FCSTD DOCUMENT  (FreeCAD 0.20R28811 (Git))
Label: Base Proto
License: All rights reserved
LicenseURL: http://en.wikipedia.org/wiki/All_rights_reserved
objects: Part::Ellipsoid×86, Part::Feature×52, Part::Fillet×44, Part::Cylinder×40, Part::MultiFuse×39, Part::Box×10, App::Part×5, Part::Wedge×1
note: 272 computed .brp shape members not serialized (recipe doc carries the construction recipe); baked Part::Feature solids carry a one-line shape summary decoded from their .brp

FEATURE [Part::Box] Box  label="Base"
  AttacherType = Attacher::AttachEngine3D
  Height = 3
  Length = 180
  Width = 120
FEATURE [Part::Box] Box001  label="Cube001"
  AttacherType = Attacher::AttachEngine3D
  Height = 10
  Length = 43
  Placement = pos=(0,0,3) rot=(0,0,1;0rad)
  Width = 3
FEATURE [Part::Box] Box002  label="Cube"
  AttacherType = Attacher::AttachEngine3D
  Height = 2.7
  Length = 43
  Placement = pos=(0,0,13) rot=(0,0,1;0rad)
  Width = 2
FEATURE [Part::Ellipsoid] Ellipsoid001
  Angle1 = -90
  Angle2 = 90
  Angle3 = 360
  AttacherType = Attacher::AttachEngine3D
  Placement = pos=(11,1.5,14.8) rot=(0,0,1;0rad)
  Radius1 = 0.5
  Radius2 = 4
  Radius3 = 0.75
FEATURE [Part::Ellipsoid] Ellipsoid002
  Angle1 = -90
  Angle2 = 90
  Angle3 = 360
  AttacherType = Attacher::AttachEngine3D
  Placement = pos=(34,1.5,14.8) rot=(0,0,1;0rad)
  Radius1 = 0.5
  Radius2 = 4
  Radius3 = 0.75
FEATURE [Part::MultiFuse] Fusion  label="Pared_RPI4_Nano"
  Refine = true
  Shapes = -> [Ellipsoid002,Box001,Box002,Ellipsoid001]
FEATURE [Part::Box] Box003  label="Cube002"
  AttacherType = Attacher::AttachEngine3D
  Height = 10
  Length = 43
  Placement = pos=(0,0,3) rot=(0,0,1;0rad)
  Width = 3
FEATURE [Part::Box] Box004  label="Cube003"
  AttacherType = Attacher::AttachEngine3D
  Height = 2.7
  Length = 43
  Placement = pos=(0,0,13) rot=(0,0,1;0rad)
  Width = 2
FEATURE [Part::Ellipsoid] Ellipsoid003
  Angle1 = -90
  Angle2 = 90
  Angle3 = 360
  AttacherType = Attacher::AttachEngine3D
  Placement = pos=(11,1.5,14.8) rot=(0,0,1;0rad)
  Radius1 = 0.5
  Radius2 = 4
  Radius3 = 0.75
FEATURE [Part::Ellipsoid] Ellipsoid004
  Angle1 = -90
  Angle2 = 90
  Angle3 = 360
  AttacherType = Attacher::AttachEngine3D
  Placement = pos=(34,1.5,14.8) rot=(0,0,1;0rad)
  Radius1 = 0.5
  Radius2 = 4
  Radius3 = 0.75
FEATURE [Part::MultiFuse] Fusion001  label="Pared_RPI4_Nano001"
  Placement = pos=(43,22,0) rot=(0,0,1;3.14159rad)
  Refine = true
  Shapes = -> [Ellipsoid004,Box003,Box004,Ellipsoid003]
FEATURE [Part::Cylinder] Cylinder001
  Angle = 360
  AttacherType = Attacher::AttachEngine3D
  FirstAngle = 0
  Height = 10
  Placement = pos=(4,4,-2) rot=(0,0,1;0rad)
  Radius = 4
  SecondAngle = 0
FEATURE [Part::Fillet] Fillet
  Base = -> Cylinder001
  Edges = 1 edges r=1: [Edge3]
  Placement = pos=(0,0,5) rot=(0,0,1;0rad)
FEATURE [Part::Cylinder] Cylinder002
  Angle = 360
  AttacherType = Attacher::AttachEngine3D
  FirstAngle = 0
  Height = 6
  Placement = pos=(5,5,18) rot=(0,0,1;0rad)
  Radius = 1.5
  SecondAngle = 0
FEATURE [Part::Cylinder] Cylinder003
  Angle = 360
  AttacherType = Attacher::AttachEngine3D
  FirstAngle = 0
  Height = 10
  Placement = pos=(4,4,-2) rot=(0,0,1;0rad)
  Radius = 4
  SecondAngle = 0
FEATURE [Part::Ellipsoid] Ellipsoid009
  Angle1 = -90
  Angle2 = 90
  Angle3 = 360
  AttacherType = Attacher::AttachEngine3D
  Placement = pos=(5,4,22) rot=(0,1,0;1.5708rad)
  Radius1 = 0.5
  Radius2 = 2
  Radius3 = 0.75
FEATURE [Part::Ellipsoid] Ellipsoid010
  Angle1 = -90
  Angle2 = 90
  Angle3 = 360
  AttacherType = Attacher::AttachEngine3D
  Placement = pos=(4,5,22) rot=(0.57735,-0.57735,-0.57735;4.18879rad)
  Radius1 = 0.5
  Radius2 = 2
  Radius3 = 0.75
FEATURE [Part::Ellipsoid] Ellipsoid011
  Angle1 = -90
  Angle2 = 90
  Angle3 = 360
  AttacherType = Attacher::AttachEngine3D
  Placement = pos=(5,6,22) rot=(0,1,0;1.5708rad)
  Radius1 = 0.5
  Radius2 = 2
  Radius3 = 0.75
FEATURE [Part::Ellipsoid] Ellipsoid012
  Angle1 = -90
  Angle2 = 90
  Angle3 = 360
  AttacherType = Attacher::AttachEngine3D
  Placement = pos=(6,5,22) rot=(0.57735,-0.57735,-0.57735;4.18879rad)
  Radius1 = 0.5
  Radius2 = 2
  Radius3 = 0.75
FEATURE [Part::Fillet] Fillet002
  Base = -> Cylinder003
  Edges = 1 edges r=1: [Edge3]
  Placement = pos=(0,0,5) rot=(0,0,1;0rad)
FEATURE [Part::MultiFuse] Fusion006
  Placement = pos=(-1,-1,-10) rot=(0,0,1;0rad)
  Refine = true
  Shapes = -> [Ellipsoid012,Cylinder002,Ellipsoid009,Ellipsoid010,Ellipsoid011]
FEATURE [Part::Fillet] Fillet003
  Base = -> Fusion006
  Edges = 1 edges r=1: [Edge7]
  Placement = pos=(0,0,4) rot=(0,0,1;0rad)
FEATURE [Part::MultiFuse] Fusion007  label="Pilar_PCB_1.6mm_3mm001"
  Placement = pos=(80,41,0) rot=(0,0,1;0rad)
  Refine = true
  Shapes = -> [Fillet003,Fillet002]
FEATURE [Part::Cylinder] Cylinder004
  Angle = 360
  AttacherType = Attacher::AttachEngine3D
  FirstAngle = 0
  Height = 6
  Placement = pos=(5,5,18) rot=(0,0,1;0rad)
  Radius = 1.5
  SecondAngle = 0
FEATURE [Part::Cylinder] Cylinder005
  Angle = 360
  AttacherType = Attacher::AttachEngine3D
  FirstAngle = 0
  Height = 10
  Placement = pos=(4,4,-2) rot=(0,0,1;0rad)
  Radius = 4
  SecondAngle = 0
FEATURE [Part::Ellipsoid] Ellipsoid013
  Angle1 = -90
  Angle2 = 90
  Angle3 = 360
  AttacherType = Attacher::AttachEngine3D
  Placement = pos=(5,4,22) rot=(0,1,0;1.5708rad)
  Radius1 = 0.5
  Radius2 = 2
  Radius3 = 0.75
FEATURE [Part::Ellipsoid] Ellipsoid014
  Angle1 = -90
  Angle2 = 90
  Angle3 = 360
  AttacherType = Attacher::AttachEngine3D
  Placement = pos=(4,5,22) rot=(0.57735,-0.57735,-0.57735;4.18879rad)
  Radius1 = 0.5
  Radius2 = 2
  Radius3 = 0.75
FEATURE [Part::Ellipsoid] Ellipsoid015
  Angle1 = -90
  Angle2 = 90
  Angle3 = 360
  AttacherType = Attacher::AttachEngine3D
  Placement = pos=(5,6,22) rot=(0,1,0;1.5708rad)
  Radius1 = 0.5
  Radius2 = 2
  Radius3 = 0.75
FEATURE [Part::Ellipsoid] Ellipsoid016
  Angle1 = -90
  Angle2 = 90
  Angle3 = 360
  AttacherType = Attacher::AttachEngine3D
  Placement = pos=(6,5,22) rot=(0.57735,-0.57735,-0.57735;4.18879rad)
  Radius1 = 0.5
  Radius2 = 2
  Radius3 = 0.75
FEATURE [Part::Fillet] Fillet004
  Base = -> Cylinder005
  Edges = 1 edges r=1: [Edge3]
  Placement = pos=(0,0,5) rot=(0,0,1;0rad)
FEATURE [Part::MultiFuse] Fusion008
  Placement = pos=(-1,-1,-10) rot=(0,0,1;0rad)
  Refine = true
  Shapes = -> [Ellipsoid016,Cylinder004,Ellipsoid013,Ellipsoid014,Ellipsoid015]
FEATURE [Part::Fillet] Fillet005
  Base = -> Fusion008
  Edges = 1 edges r=1: [Edge7]
  Placement = pos=(0,0,4) rot=(0,0,1;0rad)
FEATURE [Part::MultiFuse] Fusion009  label="Pilar_PCB_1.6mm_3mm002"
  Placement = pos=(155,10,0) rot=(0,0,1;0rad)
  Refine = true
  Shapes = -> [Fillet005,Fillet004]
FEATURE [Part::Cylinder] Cylinder006
  Angle = 360
  AttacherType = Attacher::AttachEngine3D
  FirstAngle = 0
  Height = 6
  Placement = pos=(5,5,18) rot=(0,0,1;0rad)
  Radius = 1.5
  SecondAngle = 0
FEATURE [Part::Cylinder] Cylinder007
  Angle = 360
  AttacherType = Attacher::AttachEngine3D
  FirstAngle = 0
  Height = 10
  Placement = pos=(4,4,-2) rot=(0,0,1;0rad)
  Radius = 4
  SecondAngle = 0
FEATURE [Part::Ellipsoid] Ellipsoid017
  Angle1 = -90
  Angle2 = 90
  Angle3 = 360
  AttacherType = Attacher::AttachEngine3D
  Placement = pos=(5,4,22) rot=(0,1,0;1.5708rad)
  Radius1 = 0.5
  Radius2 = 2
  Radius3 = 0.75
FEATURE [Part::Ellipsoid] Ellipsoid018
  Angle1 = -90
  Angle2 = 90
  Angle3 = 360
  AttacherType = Attacher::AttachEngine3D
  Placement = pos=(4,5,22) rot=(0.57735,-0.57735,-0.57735;4.18879rad)
  Radius1 = 0.5
  Radius2 = 2
  Radius3 = 0.75
FEATURE [Part::Ellipsoid] Ellipsoid019
  Angle1 = -90
  Angle2 = 90
  Angle3 = 360
  AttacherType = Attacher::AttachEngine3D
  Placement = pos=(5,6,22) rot=(0,1,0;1.5708rad)
  Radius1 = 0.5
  Radius2 = 2
  Radius3 = 0.75
FEATURE [Part::Ellipsoid] Ellipsoid020
  Angle1 = -90
  Angle2 = 90
  Angle3 = 360
  AttacherType = Attacher::AttachEngine3D
  Placement = pos=(6,5,22) rot=(0.57735,-0.57735,-0.57735;4.18879rad)
  Radius1 = 0.5
  Radius2 = 2
  Radius3 = 0.75
FEATURE [Part::Fillet] Fillet006
  Base = -> Cylinder007
  Edges = 1 edges r=1: [Edge3]
  Placement = pos=(0,0,5) rot=(0,0,1;0rad)
FEATURE [Part::MultiFuse] Fusion010
  Placement = pos=(-1,-1,-10) rot=(0,0,1;0rad)
  Refine = true
  Shapes = -> [Ellipsoid020,Cylinder006,Ellipsoid017,Ellipsoid018,Ellipsoid019]
FEATURE [Part::Fillet] Fillet007
  Base = -> Fusion010
  Edges = 1 edges r=1: [Edge7]
  Placement = pos=(0,0,4) rot=(0,0,1;0rad)
FEATURE [Part::MultiFuse] Fusion011  label="Pilar_PCB_1.6mm_3mm003"
  Placement = pos=(155,41,0) rot=(0,0,1;0rad)
  Refine = true
  Shapes = -> [Fillet007,Fillet006]
FEATURE [Part::Feature] Part__Feature029  label="LCD_PCB"
  Placement = pos=(-1.40554,-3.4444,3.08176) rot=(0,0,1;0rad)
  shape: bbox 80 x 1.8 x 36 mm, 166 faces (baked)
FEATURE [Part::Feature] Part__Feature030  label="metal_casing"
  Placement = pos=(-1.50554,3.0556,3.58176) rot=(0,0,1;0rad)
  shape: bbox 71.21 x 10.61 x 25.28 mm, 149 faces (baked)
FEATURE [Part::Feature] Part__Feature031  label="LCDbacklight"
  Placement = pos=(-1.75554,-3.4444,3.58176) rot=(0,0,1;0rad)
  shape: bbox 74.7 x 3 x 18 mm, 8 faces (baked)
FEATURE [Part::Feature] Part__Feature032  label="LCD"
  Placement = pos=(-1.60554,1.9556,3.58176) rot=(0,0,1;0rad)
  shape: bbox 70.3 x 2.165 x 22 mm, 5145 faces, 3 solids (baked)
FEATURE [Part::Feature] Part__Feature033  label="conductors"
  Placement = pos=(-1.75554,-0.694398,13.8318) rot=(0,0,1;0rad)
  shape: bbox 69.7 x 5.5 x 2.5 mm, 16 faces (baked)
FEATURE [Part::Feature] Part__Feature034  label="conductors001"
  Placement = pos=(-1.75554,-0.694398,-6.66824) rot=(0,0,1;0rad)
  shape: bbox 69.7 x 5.5 x 2.5 mm, 16 faces (baked)
FEATURE [Part::Feature] Part__Feature035  label="1x8 Male Pin Header"
  Placement = pos=(4.69446,-5.0444,-12.4182) rot=(0,0,1;3.14159rad)
  shape: bbox 20.33 x 13.54 x 2.5 mm, 312 faces, 9 solids (baked)
FEATURE [Part::Feature] Part__Feature036  label="1x8 Male Pin Header001"
  Placement = pos=(-33.4055,-5.0444,-12.4182) rot=(1,0,0;3.14159rad)
  shape: bbox 20.33 x 13.54 x 2.5 mm, 312 faces, 9 solids (baked)
FEATURE [Part::Feature] Part__Feature037  label="Header Female 1x16.step"
  Placement = pos=(-14.3555,-11.8719,-12.4182) rot=(0,0,1;0rad)
  shape: bbox 40.79 x 11.87 x 2.475 mm, 682 faces (baked)
FEATURE [App::Part] LCD  label="LCD001"
  Group = -> [Part__Feature029,Part__Feature030,Part__Feature031,Part__Feature032,Part__Feature033,Part__Feature034,Part__Feature035,Part__Feature036,Part__Feature037]
  Origin = -> Origin016
  Placement = pos=(123.315,30.0502,23.1551) rot=(0.999999,-0.001016,-0.001236;1.77102rad)
FEATURE [Part::Feature] Part__Feature108  label="nano-board"
  shape: bbox 43.2 x 4.77 x 18 mm, 378 faces (baked)
FEATURE [Part::Feature] Part__Feature109  label="2pin_header__02"
  Placement = pos=(-1.143,1.6,-7.62) rot=(0,0,1;0rad)
  shape: bbox 5 x 11.75 x 2.54 mm, 46 faces (baked)
FEATURE [Part::Feature] Part__Feature110  label="2pin_header__003"
  Placement = pos=(-1.143,1.6,-5.08) rot=(0,0,1;0rad)
  shape: bbox 5 x 11.75 x 2.54 mm, 46 faces (baked)
FEATURE [Part::Feature] Part__Feature111  label="2pin_header__004"
  Placement = pos=(-1.143,1.6,-10.16) rot=(0,0,1;0rad)
  shape: bbox 5 x 11.75 x 2.54 mm, 46 faces (baked)
FEATURE [Part::Feature] Part__Feature112  label="15pin_header__"
  Placement = pos=(0,0,0) rot=(0.707107,0,0.707107;3.14159rad)
  shape: bbox 38.1 x 11.75 x 2.54 mm, 364 faces (baked)
FEATURE [Part::Feature] Part__Feature113  label="15pin_header__001"
  Placement = pos=(-3e-15,0,-15.24) rot=(0.707107,0,0.707107;3.14159rad)
  shape: bbox 38.1 x 11.75 x 2.54 mm, 364 faces (baked)
FEATURE [Part::Feature] Part__Feature114  label="atmega328"
  Placement = pos=(23.85,1.75,-7.62) rot=(0,1,0;3.92699rad)
  shape: bbox 11.25 x 1.2 x 11.25 mm, 1867 faces (baked)
FEATURE [Part::Feature] Part__Feature115  label="ftdi FT232rl"
  Placement = pos=(29.05,0,-7.67) rot=(0.707107,0,-0.707107;3.14159rad)
  shape: bbox 10.2 x 1.9 x 9.287 mm, 717 faces (baked)
FEATURE [Part::Feature] Part__Feature116  label="smt_resistor222"
  Placement = pos=(21.86,0,-5.8) rot=(0.707107,0,-0.707107;3.14159rad)
  shape: bbox 3.8 x 0.6 x 1.813 mm, 74 faces (baked)
FEATURE [Part::Feature] Part__Feature117  label="smt_resistor223"
  Placement = pos=(21.86,0,-9) rot=(0.707107,0,-0.707107;3.14159rad)
  shape: bbox 3.8 x 0.6 x 1.813 mm, 74 faces (baked)
FEATURE [Part::Feature] Part__Feature118  label="smt_resistor224"
  Placement = pos=(36.75,0,-7.6) rot=(0.707107,0,-0.707107;3.14159rad)
  shape: bbox 3.8 x 0.6 x 1.813 mm, 74 faces (baked)
FEATURE [Part::Feature] Part__Feature119  label="smt_resistor225"
  Placement = pos=(36.75,0,-12) rot=(0.707107,0,-0.707107;3.14159rad)
  shape: bbox 3.8 x 0.6 x 1.813 mm, 74 faces (baked)
FEATURE [Part::Feature] Part__Feature120  label="smt_resistor226"
  Placement = pos=(8.2,0,-2.6) rot=(0.707107,0,-0.707107;3.14159rad)
  shape: bbox 3.8 x 0.6 x 1.813 mm, 74 faces (baked)
FEATURE [Part::Feature] Part__Feature121  label="led"
  Placement = pos=(10.4,1.6,-2.8) rot=(0,0,1;0rad)
  shape: bbox 4.438 x 0.8452 x 2.138 mm, 57 faces, 2 solids (baked)
FEATURE [Part::Feature] Part__Feature122  label="led001"
  Placement = pos=(10.4,1.6,-5.55) rot=(0,0,1;0rad)
  shape: bbox 4.438 x 0.8452 x 2.138 mm, 57 faces, 2 solids (baked)
FEATURE [Part::Feature] Part__Feature123  label="led002"
  Placement = pos=(10.4,1.6,-12.5) rot=(0,0,1;0rad)
  shape: bbox 4.438 x 0.8452 x 2.138 mm, 57 faces, 2 solids (baked)
FEATURE [Part::Feature] Part__Feature124  label="led003"
  Placement = pos=(10.4,1.6,-9.05) rot=(0,0,1;0rad)
  shape: bbox 4.438 x 0.8452 x 2.138 mm, 57 faces, 2 solids (baked)
FEATURE [Part::Feature] Part__Feature125  label="16mhz crystal - measured"
  Placement = pos=(18.5113,1.6,-3.55414) rot=(0,-1,0;0.785398rad)
  shape: bbox 3.394 x 0.8 x 3.394 mm, 71 faces (baked)
FEATURE [Part::Feature] Part__Feature126  label="MINIUSBSHELL"
  shape: bbox 11.03 x 3.822 x 9.475 mm, 243 faces (baked)
FEATURE [Part::Feature] Part__Feature127  label="MINIUSBCORE"
  Placement = pos=(0,0,6.7) rot=(0,1,0;3.14159rad)
  shape: bbox 7.7 x 4.5 x 8.2 mm, 127 faces (baked)
FEATURE [Part::Feature] Part__Feature128  label="MINI USB CONTACT"
  Placement = pos=(-1.6,0,5.7) rot=(0,1,0;3.14159rad)
  shape: bbox 0.5011 x 2.551 x 9.423 mm, 31 faces (baked)
FEATURE [Part::Feature] Part__Feature129  label="MINI USB CONTACT001"
  Placement = pos=(-0.8,0,5.7) rot=(0,1,0;3.14159rad)
  shape: bbox 0.5011 x 2.551 x 9.423 mm, 31 faces (baked)
FEATURE [Part::Feature] Part__Feature130  label="MINI USB CONTACT002"
  Placement = pos=(0,0,5.7) rot=(0,1,0;3.14159rad)
  shape: bbox 0.5011 x 2.551 x 9.423 mm, 31 faces (baked)
FEATURE [Part::Feature] Part__Feature131  label="MINI USB CONTACT003"
  Placement = pos=(0.8,0,5.7) rot=(0,1,0;3.14159rad)
  shape: bbox 0.5011 x 2.551 x 9.423 mm, 31 faces (baked)
FEATURE [Part::Feature] Part__Feature132  label="MINI USB CONTACT004"
  Placement = pos=(1.6,0,5.7) rot=(0,1,0;3.14159rad)
  shape: bbox 0.5011 x 2.551 x 9.423 mm, 31 faces (baked)
FEATURE [App::Part] MINIUSB___MEASURED  label="MINIUSB - MEASURED"
  Group = -> [Part__Feature126,Part__Feature127,Part__Feature128,Part__Feature129,Part__Feature130,Part__Feature131,Part__Feature132]
  Origin = -> Origin019
  Placement = pos=(38.98,1.65,-7.62) rot=(0,-1,0;1.5708rad)
FEATURE [Part::Feature] Part__Feature133  label="cap106C"
  Placement = pos=(37.2,0,-3.3) rot=(0.707107,0,0.707107;3.14159rad)
  shape: bbox 4.001 x 1.811 x 1.701 mm, 124 faces (baked)
FEATURE [Part::Feature] Part__Feature134  label="cap106C001"
  Placement = pos=(7.9,-1e-15,-5.6) rot=(0.707107,0,-0.707107;3.14159rad)
  shape: bbox 4.001 x 1.811 x 1.701 mm, 124 faces (baked)
FEATURE [Part::Feature] Part__Feature135  label="reset core"
  shape: bbox 5.2 x 2.15 x 2.8 mm, 77 faces (baked)
FEATURE [Part::Feature] Part__Feature136  label="reset shell"
  Placement = pos=(0,1.65,0) rot=(0,-1,0;1.5708rad)
  shape: bbox 4 x 1.65 x 3 mm, 100 faces (baked)
FEATURE [Part::Feature] Part__Feature137  label="nano - reg"
  Placement = pos=(6.1,0,-10.16) rot=(0.707107,0,-0.707107;3.14159rad)
  shape: bbox 8.3 x 1.689 x 6.5 mm, 198 faces (baked)
FEATURE [Part::Feature] Part__Feature138  label="NANO DIODE"
  Placement = pos=(11.43,0,-4.2) rot=(0.707107,0,0.707107;3.14159rad)
  shape: bbox 1.7 x 1.384 x 4.916 mm, 85 faces (baked)
FEATURE [Part::Feature] Part__Feature139  label="189 RESISTOR PACK"
  Placement = pos=(15.75,0,-10.85) rot=(0.707107,0,0.707107;3.14159rad)
  shape: bbox 3 x 0.5573 x 3.2 mm, 288 faces, 10 solids (baked)
FEATURE [Part::Feature] Part__Feature140  label="102 RESISTOR PACK"
  Placement = pos=(15.75,0,-5.2) rot=(0.707107,0,0.707107;3.14159rad)
  shape: bbox 3 x 0.5573 x 3.2 mm, 277 faces, 10 solids (baked)
FEATURE [App::Part] reset_button  label="reset button"
  Group = -> [Part__Feature135,Part__Feature136]
  Origin = -> Origin020
  Placement = pos=(15.25,1.6,-8.05) rot=(0,1,0;1.5708rad)
FEATURE [App::Part] arduino_nano  label="arduino nano"
  Group = -> [Part__Feature108,Part__Feature109,Part__Feature110,Part__Feature111,Part__Feature112,Part__Feature113,Part__Feature114,Part__Feature115,Part__Feature116,Part__Feature117,Part__Feature118,Part__Feature119,Part__Feature120,Part__Feature121,Part__Feature122,Part__Feature123,Part__Feature124,Part__Feature125,MINIUSB___MEASURED,Part__Feature133,Part__Feature134,reset_button,Part__Feature137,+3 more]
  Origin = -> Origin021
  Placement = pos=(54.5,38.6,13) rot=(0,0.707107,0.707107;3.14159rad)
FEATURE [Part::MultiFuse] Fusion013  label="Suports_Arduino_Nano"
  Placement = pos=(15,20,0) rot=(0,0,1;0rad)
  Refine = true
  Shapes = -> [Fusion001,Fusion]
FEATURE [Part::Wedge] Wedge
  AttacherType = Attacher::AttachEngine3D
  Placement = pos=(75,7,3) rot=(0,0,1;0rad)
  X2max = 95
  X2min = 0
  Xmax = 95
  Xmin = 0
  Ymax = 45
  Ymin = 0
  Z2max = 10
  Z2min = 0
  Zmax = 1
  Zmin = 0
FEATURE [Part::Box] Box006  label="Cube005"
  AttacherType = Attacher::AttachEngine3D
  Height = 10
  Length = 20
  Placement = pos=(0,0,3) rot=(0,0,1;0rad)
  Width = 3
FEATURE [Part::Box] Box007  label="Cube006"
  AttacherType = Attacher::AttachEngine3D
  Height = 3
  Length = 20
  Placement = pos=(0,0,13) rot=(0,0,1;0rad)
  Width = 2
FEATURE [Part::Ellipsoid] Ellipsoid021
  Angle1 = -90
  Angle2 = 90
  Angle3 = 360
  AttacherType = Attacher::AttachEngine3D
  Placement = pos=(10,1.5,14.8) rot=(0,0,1;0rad)
  Radius1 = 0.5
  Radius2 = 4
  Radius3 = 0.75
FEATURE [Part::MultiFuse] Fusion014
  Placement = pos=(20,74,0) rot=(0,0,1;3.14159rad)
  Refine = true
  Shapes = -> [Box006,Box007,Ellipsoid021]
FEATURE [Part::Box] Box008  label="Cube007"
  AttacherType = Attacher::AttachEngine3D
  Height = 10
  Length = 20
  Placement = pos=(0,0,3) rot=(0,0,1;0rad)
  Width = 3
FEATURE [Part::Box] Box009  label="Cube008"
  AttacherType = Attacher::AttachEngine3D
  Height = 3
  Length = 20
  Placement = pos=(0,0,13) rot=(0,0,1;0rad)
  Width = 2
FEATURE [Part::Ellipsoid] Ellipsoid023
  Angle1 = -90
  Angle2 = 90
  Angle3 = 360
  AttacherType = Attacher::AttachEngine3D
  Placement = pos=(10,1.5,14.8) rot=(0,0,1;0rad)
  Radius1 = 0.5
  Radius2 = 4
  Radius3 = 0.75
FEATURE [Part::Cylinder] Cylinder
  Angle = 360
  AttacherType = Attacher::AttachEngine3D
  FirstAngle = 0
  Height = 6
  Placement = pos=(5,5,18) rot=(0,0,1;0rad)
  Radius = 1.5
  SecondAngle = 0
FEATURE [Part::Ellipsoid] Ellipsoid005
  Angle1 = -90
  Angle2 = 90
  Angle3 = 360
  AttacherType = Attacher::AttachEngine3D
  Placement = pos=(5,4,22) rot=(0,1,0;1.5708rad)
  Radius1 = 0.5
  Radius2 = 2
  Radius3 = 0.75
FEATURE [Part::Ellipsoid] Ellipsoid006
  Angle1 = -90
  Angle2 = 90
  Angle3 = 360
  AttacherType = Attacher::AttachEngine3D
  Placement = pos=(4,5,22) rot=(0.57735,-0.57735,-0.57735;4.18879rad)
  Radius1 = 0.5
  Radius2 = 2
  Radius3 = 0.75
FEATURE [Part::Ellipsoid] Ellipsoid007
  Angle1 = -90
  Angle2 = 90
  Angle3 = 360
  AttacherType = Attacher::AttachEngine3D
  Placement = pos=(5,6,22) rot=(0,1,0;1.5708rad)
  Radius1 = 0.5
  Radius2 = 2
  Radius3 = 0.75
FEATURE [Part::Ellipsoid] Ellipsoid008
  Angle1 = -90
  Angle2 = 90
  Angle3 = 360
  AttacherType = Attacher::AttachEngine3D
  Placement = pos=(6,5,22) rot=(0.57735,-0.57735,-0.57735;4.18879rad)
  Radius1 = 0.5
  Radius2 = 2
  Radius3 = 0.75
FEATURE [Part::MultiFuse] Fusion004
  Placement = pos=(-1,-1,-10) rot=(0,0,1;0rad)
  Refine = true
  Shapes = -> [Ellipsoid008,Cylinder,Ellipsoid005,Ellipsoid006,Ellipsoid007]
FEATURE [Part::Fillet] Fillet001
  Base = -> Fusion004
  Edges = 1 edges r=1: [Edge7]
  Placement = pos=(0,0,4) rot=(0,0,1;0rad)
FEATURE [Part::MultiFuse] Fusion005  label="Pilar_PCB_1.6mm_3mm"
  Placement = pos=(80,10,0) rot=(0,0,1;0rad)
  Refine = true
  Shapes = -> [Fillet001,Fillet]
FEATURE [Part::MultiFuse] Fusion012  label="Pilars_LCD"
  Placement = pos=(0.759155,1.60425,-0.930457) rot=(0.999724,-0.023102,0.004189;0.197397rad)
  Refine = true
  Shapes = -> [Fusion005,Fusion007,Fusion009,Fusion011]
FEATURE [Part::MultiFuse] Fusion003
  Placement = pos=(-5,0,0) rot=(0,0,1;0rad)
  Refine = true
  Shapes = -> [Ellipsoid008,Cylinder,Ellipsoid005,Ellipsoid006,Ellipsoid007]
FEATURE [Part::Cylinder] Cylinder008
  Angle = 360
  AttacherType = Attacher::AttachEngine3D
  FirstAngle = 0
  Height = 6
  Placement = pos=(5,5,18) rot=(0,0,1;0rad)
  Radius = 1.5
  SecondAngle = 0
FEATURE [Part::Cylinder] Cylinder009
  Angle = 360
  AttacherType = Attacher::AttachEngine3D
  FirstAngle = 0
  Height = 10
  Placement = pos=(4,4,-2) rot=(0,0,1;0rad)
  Radius = 4
  SecondAngle = 0
FEATURE [Part::Ellipsoid] Ellipsoid025
  Angle1 = -90
  Angle2 = 90
  Angle3 = 360
  AttacherType = Attacher::AttachEngine3D
  Placement = pos=(5,4,22) rot=(0,1,0;1.5708rad)
  Radius1 = 0.5
  Radius2 = 2
  Radius3 = 0.75
FEATURE [Part::Ellipsoid] Ellipsoid026
  Angle1 = -90
  Angle2 = 90
  Angle3 = 360
  AttacherType = Attacher::AttachEngine3D
  Placement = pos=(4,5,22) rot=(0.57735,-0.57735,-0.57735;4.18879rad)
  Radius1 = 0.5
  Radius2 = 2
  Radius3 = 0.75
FEATURE [Part::Ellipsoid] Ellipsoid027
  Angle1 = -90
  Angle2 = 90
  Angle3 = 360
  AttacherType = Attacher::AttachEngine3D
  Placement = pos=(5,6,22) rot=(0,1,0;1.5708rad)
  Radius1 = 0.5
  Radius2 = 2
  Radius3 = 0.75
FEATURE [Part::Ellipsoid] Ellipsoid028
  Angle1 = -90
  Angle2 = 90
  Angle3 = 360
  AttacherType = Attacher::AttachEngine3D
  Placement = pos=(6,5,22) rot=(0.57735,-0.57735,-0.57735;4.18879rad)
  Radius1 = 0.5
  Radius2 = 2
  Radius3 = 0.75
FEATURE [Part::Fillet] Fillet008
  Base = -> Cylinder009
  Edges = 1 edges r=1: [Edge3]
  Placement = pos=(0,0,5) rot=(0,0,1;0rad)
FEATURE [Part::MultiFuse] Fusion017
  Placement = pos=(-1,-1,-10) rot=(0,0,1;0rad)
  Refine = true
  Shapes = -> [Ellipsoid028,Cylinder008,Ellipsoid025,Ellipsoid026,Ellipsoid027]
FEATURE [Part::Fillet] Fillet009
  Base = -> Fusion017
  Edges = 1 edges r=1: [Edge7]
  Placement = pos=(0,0,4) rot=(0,0,1;0rad)
FEATURE [Part::Cylinder] Cylinder010
  Angle = 360
  AttacherType = Attacher::AttachEngine3D
  FirstAngle = 0
  Height = 6
  Placement = pos=(5,5,18) rot=(0,0,1;0rad)
  Radius = 1.5
  SecondAngle = 0
FEATURE [Part::Cylinder] Cylinder011
  Angle = 360
  AttacherType = Attacher::AttachEngine3D
  FirstAngle = 0
  Height = 10
  Placement = pos=(4,4,-2) rot=(0,0,1;0rad)
  Radius = 4
  SecondAngle = 0
FEATURE [Part::Ellipsoid] Ellipsoid029
  Angle1 = -90
  Angle2 = 90
  Angle3 = 360
  AttacherType = Attacher::AttachEngine3D
  Placement = pos=(5,4,22) rot=(0,1,0;1.5708rad)
  Radius1 = 0.5
  Radius2 = 2
  Radius3 = 0.75
FEATURE [Part::Ellipsoid] Ellipsoid030
  Angle1 = -90
  Angle2 = 90
  Angle3 = 360
  AttacherType = Attacher::AttachEngine3D
  Placement = pos=(4,5,22) rot=(0.57735,-0.57735,-0.57735;4.18879rad)
  Radius1 = 0.5
  Radius2 = 2
  Radius3 = 0.75
FEATURE [Part::Ellipsoid] Ellipsoid031
  Angle1 = -90
  Angle2 = 90
  Angle3 = 360
  AttacherType = Attacher::AttachEngine3D
  Placement = pos=(5,6,22) rot=(0,1,0;1.5708rad)
  Radius1 = 0.5
  Radius2 = 2
  Radius3 = 0.75
FEATURE [Part::Ellipsoid] Ellipsoid032
  Angle1 = -90
  Angle2 = 90
  Angle3 = 360
  AttacherType = Attacher::AttachEngine3D
  Placement = pos=(6,5,22) rot=(0.57735,-0.57735,-0.57735;4.18879rad)
  Radius1 = 0.5
  Radius2 = 2
  Radius3 = 0.75
FEATURE [Part::Fillet] Fillet010
  Base = -> Cylinder011
  Edges = 1 edges r=1: [Edge3]
  Placement = pos=(0,0,5) rot=(0,0,1;0rad)
FEATURE [Part::MultiFuse] Fusion019
  Placement = pos=(-1,-1,-10) rot=(0,0,1;0rad)
  Refine = true
  Shapes = -> [Ellipsoid032,Cylinder010,Ellipsoid029,Ellipsoid030,Ellipsoid031]
FEATURE [Part::Fillet] Fillet011
  Base = -> Fusion019
  Edges = 1 edges r=1: [Edge7]
  Placement = pos=(0,0,4) rot=(0,0,1;0rad)
FEATURE [Part::Cylinder] Cylinder012
  Angle = 360
  AttacherType = Attacher::AttachEngine3D
  FirstAngle = 0
  Height = 6
  Placement = pos=(5,5,18) rot=(0,0,1;0rad)
  Radius = 1.5
  SecondAngle = 0
FEATURE [Part::Cylinder] Cylinder013
  Angle = 360
  AttacherType = Attacher::AttachEngine3D
  FirstAngle = 0
  Height = 10
  Placement = pos=(4,4,-2) rot=(0,0,1;0rad)
  Radius = 4
  SecondAngle = 0
FEATURE [Part::Cylinder] Cylinder014
  Angle = 360
  AttacherType = Attacher::AttachEngine3D
  FirstAngle = 0
  Height = 6
  Placement = pos=(5,5,18) rot=(0,0,1;0rad)
  Radius = 1.5
  SecondAngle = 0
FEATURE [Part::Cylinder] Cylinder015
  Angle = 360
  AttacherType = Attacher::AttachEngine3D
  FirstAngle = 0
  Height = 10
  Placement = pos=(4,4,-2) rot=(0,0,1;0rad)
  Radius = 4
  SecondAngle = 0
FEATURE [Part::Ellipsoid] Ellipsoid033
  Angle1 = -90
  Angle2 = 90
  Angle3 = 360
  AttacherType = Attacher::AttachEngine3D
  Placement = pos=(5,4,22) rot=(0,1,0;1.5708rad)
  Radius1 = 0.5
  Radius2 = 2
  Radius3 = 0.75
FEATURE [Part::Ellipsoid] Ellipsoid034
  Angle1 = -90
  Angle2 = 90
  Angle3 = 360
  AttacherType = Attacher::AttachEngine3D
  Placement = pos=(4,5,22) rot=(0.57735,-0.57735,-0.57735;4.18879rad)
  Radius1 = 0.5
  Radius2 = 2
  Radius3 = 0.75
FEATURE [Part::Ellipsoid] Ellipsoid035
  Angle1 = -90
  Angle2 = 90
  Angle3 = 360
  AttacherType = Attacher::AttachEngine3D
  Placement = pos=(5,6,22) rot=(0,1,0;1.5708rad)
  Radius1 = 0.5
  Radius2 = 2
  Radius3 = 0.75
FEATURE [Part::Ellipsoid] Ellipsoid036
  Angle1 = -90
  Angle2 = 90
  Angle3 = 360
  AttacherType = Attacher::AttachEngine3D
  Placement = pos=(6,5,22) rot=(0.57735,-0.57735,-0.57735;4.18879rad)
  Radius1 = 0.5
  Radius2 = 2
  Radius3 = 0.75
FEATURE [Part::Ellipsoid] Ellipsoid037
  Angle1 = -90
  Angle2 = 90
  Angle3 = 360
  AttacherType = Attacher::AttachEngine3D
  Placement = pos=(5,4,22) rot=(0,1,0;1.5708rad)
  Radius1 = 0.5
  Radius2 = 2
  Radius3 = 0.75
FEATURE [Part::Ellipsoid] Ellipsoid038
  Angle1 = -90
  Angle2 = 90
  Angle3 = 360
  AttacherType = Attacher::AttachEngine3D
  Placement = pos=(4,5,22) rot=(0.57735,-0.57735,-0.57735;4.18879rad)
  Radius1 = 0.5
  Radius2 = 2
  Radius3 = 0.75
FEATURE [Part::Ellipsoid] Ellipsoid039
  Angle1 = -90
  Angle2 = 90
  Angle3 = 360
  AttacherType = Attacher::AttachEngine3D
  Placement = pos=(5,6,22) rot=(0,1,0;1.5708rad)
  Radius1 = 0.5
  Radius2 = 2
  Radius3 = 0.75
FEATURE [Part::Ellipsoid] Ellipsoid040
  Angle1 = -90
  Angle2 = 90
  Angle3 = 360
  AttacherType = Attacher::AttachEngine3D
  Placement = pos=(6,5,22) rot=(0.57735,-0.57735,-0.57735;4.18879rad)
  Radius1 = 0.5
  Radius2 = 2
  Radius3 = 0.75
FEATURE [Part::Fillet] Fillet012
  Base = -> Cylinder013
  Edges = 1 edges r=1: [Edge3]
  Placement = pos=(0,0,5) rot=(0,0,1;0rad)
FEATURE [Part::Fillet] Fillet014
  Base = -> Cylinder015
  Edges = 1 edges r=1: [Edge3]
  Placement = pos=(0,0,5) rot=(0,0,1;0rad)
FEATURE [Part::MultiFuse] Fusion021
  Placement = pos=(-1,-1,-10) rot=(0,0,1;0rad)
  Refine = true
  Shapes = -> [Ellipsoid036,Cylinder012,Ellipsoid033,Ellipsoid034,Ellipsoid035]
FEATURE [Part::Fillet] Fillet013
  Base = -> Fusion021
  Edges = 1 edges r=1: [Edge7]
  Placement = pos=(0,0,4) rot=(0,0,1;0rad)
FEATURE [Part::MultiFuse] Fusion023
  Placement = pos=(-1,-1,-10) rot=(0,0,1;0rad)
  Refine = true
  Shapes = -> [Ellipsoid040,Cylinder014,Ellipsoid037,Ellipsoid038,Ellipsoid039]
FEATURE [Part::Fillet] Fillet015
  Base = -> Fusion023
  Edges = 1 edges r=1: [Edge7]
  Placement = pos=(0,0,4) rot=(0,0,1;0rad)
FEATURE [Part::MultiFuse] Fusion026
  Refine = true
  Shapes = -> [Wedge,Fusion012]
FEATURE [Part::Fillet] Fillet016  label="Support_LCD_2004"
  Base = -> Fusion026
  Edges = 4 edges r=1: [Edge10,Edge11,Edge12,Edge13]
FEATURE [Part::MultiFuse] Fusion027  label="Pilar_PCB_1.6mm_3mm004"
  Placement = pos=(28,0,0) rot=(0,0,1;0rad)
  Refine = true
  Shapes = -> [Fillet008,Fillet009,Fillet010,Fillet011,Fillet012,Fillet013,Fillet014,Fillet015]
FEATURE [Part::Cylinder] Cylinder016
  Angle = 360
  AttacherType = Attacher::AttachEngine3D
  FirstAngle = 0
  Height = 6
  Placement = pos=(5,5,18) rot=(0,0,1;0rad)
  Radius = 1.5
  SecondAngle = 0
FEATURE [Part::Cylinder] Cylinder017
  Angle = 360
  AttacherType = Attacher::AttachEngine3D
  FirstAngle = 0
  Height = 10
  Placement = pos=(4,4,-2) rot=(0,0,1;0rad)
  Radius = 4
  SecondAngle = 0
FEATURE [Part::Cylinder] Cylinder018
  Angle = 360
  AttacherType = Attacher::AttachEngine3D
  FirstAngle = 0
  Height = 6
  Placement = pos=(5,5,18) rot=(0,0,1;0rad)
  Radius = 1.5
  SecondAngle = 0
FEATURE [Part::Cylinder] Cylinder019
  Angle = 360
  AttacherType = Attacher::AttachEngine3D
  FirstAngle = 0
  Height = 10
  Placement = pos=(4,4,-2) rot=(0,0,1;0rad)
  Radius = 4
  SecondAngle = 0
FEATURE [Part::Cylinder] Cylinder020
  Angle = 360
  AttacherType = Attacher::AttachEngine3D
  FirstAngle = 0
  Height = 6
  Placement = pos=(5,5,18) rot=(0,0,1;0rad)
  Radius = 1.5
  SecondAngle = 0
FEATURE [Part::Cylinder] Cylinder021
  Angle = 360
  AttacherType = Attacher::AttachEngine3D
  FirstAngle = 0
  Height = 10
  Placement = pos=(4,4,-2) rot=(0,0,1;0rad)
  Radius = 4
  SecondAngle = 0
FEATURE [Part::Cylinder] Cylinder022
  Angle = 360
  AttacherType = Attacher::AttachEngine3D
  FirstAngle = 0
  Height = 6
  Placement = pos=(5,5,18) rot=(0,0,1;0rad)
  Radius = 1.5
  SecondAngle = 0
FEATURE [Part::Cylinder] Cylinder023
  Angle = 360
  AttacherType = Attacher::AttachEngine3D
  FirstAngle = 0
  Height = 10
  Placement = pos=(4,4,-2) rot=(0,0,1;0rad)
  Radius = 4
  SecondAngle = 0
FEATURE [Part::Ellipsoid] Ellipsoid041
  Angle1 = -90
  Angle2 = 90
  Angle3 = 360
  AttacherType = Attacher::AttachEngine3D
  Placement = pos=(5,4,22) rot=(0,1,0;1.5708rad)
  Radius1 = 0.5
  Radius2 = 2
  Radius3 = 0.75
FEATURE [Part::Ellipsoid] Ellipsoid042
  Angle1 = -90
  Angle2 = 90
  Angle3 = 360
  AttacherType = Attacher::AttachEngine3D
  Placement = pos=(4,5,22) rot=(0.57735,-0.57735,-0.57735;4.18879rad)
  Radius1 = 0.5
  Radius2 = 2
  Radius3 = 0.75
FEATURE [Part::Ellipsoid] Ellipsoid043
  Angle1 = -90
  Angle2 = 90
  Angle3 = 360
  AttacherType = Attacher::AttachEngine3D
  Placement = pos=(5,6,22) rot=(0,1,0;1.5708rad)
  Radius1 = 0.5
  Radius2 = 2
  Radius3 = 0.75
FEATURE [Part::Ellipsoid] Ellipsoid044
  Angle1 = -90
  Angle2 = 90
  Angle3 = 360
  AttacherType = Attacher::AttachEngine3D
  Placement = pos=(6,5,22) rot=(0.57735,-0.57735,-0.57735;4.18879rad)
  Radius1 = 0.5
  Radius2 = 2
  Radius3 = 0.75
FEATURE [Part::Ellipsoid] Ellipsoid045
  Angle1 = -90
  Angle2 = 90
  Angle3 = 360
  AttacherType = Attacher::AttachEngine3D
  Placement = pos=(5,4,22) rot=(0,1,0;1.5708rad)
  Radius1 = 0.5
  Radius2 = 2
  Radius3 = 0.75
FEATURE [Part::Ellipsoid] Ellipsoid046
  Angle1 = -90
  Angle2 = 90
  Angle3 = 360
  AttacherType = Attacher::AttachEngine3D
  Placement = pos=(4,5,22) rot=(0.57735,-0.57735,-0.57735;4.18879rad)
  Radius1 = 0.5
  Radius2 = 2
  Radius3 = 0.75
FEATURE [Part::Ellipsoid] Ellipsoid047
  Angle1 = -90
  Angle2 = 90
  Angle3 = 360
  AttacherType = Attacher::AttachEngine3D
  Placement = pos=(5,6,22) rot=(0,1,0;1.5708rad)
  Radius1 = 0.5
  Radius2 = 2
  Radius3 = 0.75
FEATURE [Part::Ellipsoid] Ellipsoid048
  Angle1 = -90
  Angle2 = 90
  Angle3 = 360
  AttacherType = Attacher::AttachEngine3D
  Placement = pos=(6,5,22) rot=(0.57735,-0.57735,-0.57735;4.18879rad)
  Radius1 = 0.5
  Radius2 = 2
  Radius3 = 0.75
FEATURE [Part::Ellipsoid] Ellipsoid049
  Angle1 = -90
  Angle2 = 90
  Angle3 = 360
  AttacherType = Attacher::AttachEngine3D
  Placement = pos=(5,4,22) rot=(0,1,0;1.5708rad)
  Radius1 = 0.5
  Radius2 = 2
  Radius3 = 0.75
FEATURE [Part::Ellipsoid] Ellipsoid050
  Angle1 = -90
  Angle2 = 90
  Angle3 = 360
  AttacherType = Attacher::AttachEngine3D
  Placement = pos=(4,5,22) rot=(0.57735,-0.57735,-0.57735;4.18879rad)
  Radius1 = 0.5
  Radius2 = 2
  Radius3 = 0.75
FEATURE [Part::Ellipsoid] Ellipsoid051
  Angle1 = -90
  Angle2 = 90
  Angle3 = 360
  AttacherType = Attacher::AttachEngine3D
  Placement = pos=(5,6,22) rot=(0,1,0;1.5708rad)
  Radius1 = 0.5
  Radius2 = 2
  Radius3 = 0.75
FEATURE [Part::Ellipsoid] Ellipsoid052
  Angle1 = -90
  Angle2 = 90
  Angle3 = 360
  AttacherType = Attacher::AttachEngine3D
  Placement = pos=(6,5,22) rot=(0.57735,-0.57735,-0.57735;4.18879rad)
  Radius1 = 0.5
  Radius2 = 2
  Radius3 = 0.75
FEATURE [Part::Ellipsoid] Ellipsoid053
  Angle1 = -90
  Angle2 = 90
  Angle3 = 360
  AttacherType = Attacher::AttachEngine3D
  Placement = pos=(5,4,22) rot=(0,1,0;1.5708rad)
  Radius1 = 0.5
  Radius2 = 2
  Radius3 = 0.75
FEATURE [Part::Ellipsoid] Ellipsoid054
  Angle1 = -90
  Angle2 = 90
  Angle3 = 360
  AttacherType = Attacher::AttachEngine3D
  Placement = pos=(4,5,22) rot=(0.57735,-0.57735,-0.57735;4.18879rad)
  Radius1 = 0.5
  Radius2 = 2
  Radius3 = 0.75
FEATURE [Part::Ellipsoid] Ellipsoid055
  Angle1 = -90
  Angle2 = 90
  Angle3 = 360
  AttacherType = Attacher::AttachEngine3D
  Placement = pos=(5,6,22) rot=(0,1,0;1.5708rad)
  Radius1 = 0.5
  Radius2 = 2
  Radius3 = 0.75
FEATURE [Part::Ellipsoid] Ellipsoid056
  Angle1 = -90
  Angle2 = 90
  Angle3 = 360
  AttacherType = Attacher::AttachEngine3D
  Placement = pos=(6,5,22) rot=(0.57735,-0.57735,-0.57735;4.18879rad)
  Radius1 = 0.5
  Radius2 = 2
  Radius3 = 0.75
FEATURE [Part::Fillet] Fillet017
  Base = -> Cylinder017
  Edges = 1 edges r=1: [Edge3]
  Placement = pos=(0,0,5) rot=(0,0,1;0rad)
FEATURE [Part::Fillet] Fillet019
  Base = -> Cylinder019
  Edges = 1 edges r=1: [Edge3]
  Placement = pos=(0,0,5) rot=(0,0,1;0rad)
FEATURE [Part::Fillet] Fillet021
  Base = -> Cylinder021
  Edges = 1 edges r=1: [Edge3]
  Placement = pos=(0,0,5) rot=(0,0,1;0rad)
FEATURE [Part::Fillet] Fillet023
  Base = -> Cylinder023
  Edges = 1 edges r=1: [Edge3]
  Placement = pos=(0,0,5) rot=(0,0,1;0rad)
FEATURE [Part::MultiFuse] Fusion028
  Placement = pos=(-1,-1,-10) rot=(0,0,1;0rad)
  Refine = true
  Shapes = -> [Ellipsoid044,Cylinder016,Ellipsoid041,Ellipsoid042,Ellipsoid043]
FEATURE [Part::Fillet] Fillet018
  Base = -> Fusion028
  Edges = 1 edges r=1: [Edge7]
  Placement = pos=(0,0,4) rot=(0,0,1;0rad)
FEATURE [Part::MultiFuse] Fusion029
  Placement = pos=(-1,-1,-10) rot=(0,0,1;0rad)
  Refine = true
  Shapes = -> [Ellipsoid048,Cylinder018,Ellipsoid045,Ellipsoid046,Ellipsoid047]
FEATURE [Part::Fillet] Fillet020
  Base = -> Fusion029
  Edges = 1 edges r=1: [Edge7]
  Placement = pos=(0,0,4) rot=(0,0,1;0rad)
FEATURE [Part::MultiFuse] Fusion030
  Placement = pos=(-1,-1,-10) rot=(0,0,1;0rad)
  Refine = true
  Shapes = -> [Ellipsoid052,Cylinder020,Ellipsoid049,Ellipsoid050,Ellipsoid051]
FEATURE [Part::Fillet] Fillet022
  Base = -> Fusion030
  Edges = 1 edges r=1: [Edge7]
  Placement = pos=(0,0,4) rot=(0,0,1;0rad)
FEATURE [Part::MultiFuse] Fusion031
  Placement = pos=(-1,-1,-10) rot=(0,0,1;0rad)
  Refine = true
  Shapes = -> [Ellipsoid056,Cylinder022,Ellipsoid053,Ellipsoid054,Ellipsoid055]
FEATURE [Part::Fillet] Fillet024
  Base = -> Fusion031
  Edges = 1 edges r=1: [Edge7]
  Placement = pos=(0,0,4) rot=(0,0,1;0rad)
FEATURE [Part::MultiFuse] Fusion032  label="Pilar_PCB_1.6mm_3mm005"
  Placement = pos=(28,20,0) rot=(0,0,1;0rad)
  Refine = true
  Shapes = -> [Fillet017,Fillet018,Fillet019,Fillet020,Fillet021,Fillet022,Fillet023,Fillet024]
FEATURE [Part::Cylinder] Cylinder024
  Angle = 360
  AttacherType = Attacher::AttachEngine3D
  FirstAngle = 0
  Height = 6
  Placement = pos=(5,5,18) rot=(0,0,1;0rad)
  Radius = 1.5
  SecondAngle = 0
FEATURE [Part::Cylinder] Cylinder025
  Angle = 360
  AttacherType = Attacher::AttachEngine3D
  FirstAngle = 0
  Height = 10
  Placement = pos=(4,4,-2) rot=(0,0,1;0rad)
  Radius = 4
  SecondAngle = 0
FEATURE [Part::Cylinder] Cylinder026
  Angle = 360
  AttacherType = Attacher::AttachEngine3D
  FirstAngle = 0
  Height = 6
  Placement = pos=(5,5,18) rot=(0,0,1;0rad)
  Radius = 1.5
  SecondAngle = 0
FEATURE [Part::Cylinder] Cylinder027
  Angle = 360
  AttacherType = Attacher::AttachEngine3D
  FirstAngle = 0
  Height = 10
  Placement = pos=(4,4,-2) rot=(0,0,1;0rad)
  Radius = 4
  SecondAngle = 0
FEATURE [Part::Cylinder] Cylinder028
  Angle = 360
  AttacherType = Attacher::AttachEngine3D
  FirstAngle = 0
  Height = 6
  Placement = pos=(5,5,18) rot=(0,0,1;0rad)
  Radius = 1.5
  SecondAngle = 0
FEATURE [Part::Cylinder] Cylinder029
  Angle = 360
  AttacherType = Attacher::AttachEngine3D
  FirstAngle = 0
  Height = 10
  Placement = pos=(4,4,-2) rot=(0,0,1;0rad)
  Radius = 4
  SecondAngle = 0
FEATURE [Part::Cylinder] Cylinder030
  Angle = 360
  AttacherType = Attacher::AttachEngine3D
  FirstAngle = 0
  Height = 6
  Placement = pos=(5,5,18) rot=(0,0,1;0rad)
  Radius = 1.5
  SecondAngle = 0
FEATURE [Part::Cylinder] Cylinder031
  Angle = 360
  AttacherType = Attacher::AttachEngine3D
  FirstAngle = 0
  Height = 10
  Placement = pos=(4,4,-2) rot=(0,0,1;0rad)
  Radius = 4
  SecondAngle = 0
FEATURE [Part::Cylinder] Cylinder032
  Angle = 360
  AttacherType = Attacher::AttachEngine3D
  FirstAngle = 0
  Height = 6
  Placement = pos=(5,5,18) rot=(0,0,1;0rad)
  Radius = 1.5
  SecondAngle = 0
FEATURE [Part::Cylinder] Cylinder033
  Angle = 360
  AttacherType = Attacher::AttachEngine3D
  FirstAngle = 0
  Height = 10
  Placement = pos=(4,4,-2) rot=(0,0,1;0rad)
  Radius = 4
  SecondAngle = 0
FEATURE [Part::Cylinder] Cylinder034
  Angle = 360
  AttacherType = Attacher::AttachEngine3D
  FirstAngle = 0
  Height = 6
  Placement = pos=(5,5,18) rot=(0,0,1;0rad)
  Radius = 1.5
  SecondAngle = 0
FEATURE [Part::Cylinder] Cylinder035
  Angle = 360
  AttacherType = Attacher::AttachEngine3D
  FirstAngle = 0
  Height = 10
  Placement = pos=(4,4,-2) rot=(0,0,1;0rad)
  Radius = 4
  SecondAngle = 0
FEATURE [Part::Cylinder] Cylinder036
  Angle = 360
  AttacherType = Attacher::AttachEngine3D
  FirstAngle = 0
  Height = 6
  Placement = pos=(5,5,18) rot=(0,0,1;0rad)
  Radius = 1.5
  SecondAngle = 0
FEATURE [Part::Cylinder] Cylinder037
  Angle = 360
  AttacherType = Attacher::AttachEngine3D
  FirstAngle = 0
  Height = 10
  Placement = pos=(4,4,-2) rot=(0,0,1;0rad)
  Radius = 4
  SecondAngle = 0
FEATURE [Part::Cylinder] Cylinder038
  Angle = 360
  AttacherType = Attacher::AttachEngine3D
  FirstAngle = 0
  Height = 6
  Placement = pos=(5,5,18) rot=(0,0,1;0rad)
  Radius = 1.5
  SecondAngle = 0
FEATURE [Part::Cylinder] Cylinder039
  Angle = 360
  AttacherType = Attacher::AttachEngine3D
  FirstAngle = 0
  Height = 10
  Placement = pos=(4,4,-2) rot=(0,0,1;0rad)
  Radius = 4
  SecondAngle = 0
FEATURE [Part::Ellipsoid] Ellipsoid057
  Angle1 = -90
  Angle2 = 90
  Angle3 = 360
  AttacherType = Attacher::AttachEngine3D
  Placement = pos=(5,4,22) rot=(0,1,0;1.5708rad)
  Radius1 = 0.5
  Radius2 = 2
  Radius3 = 0.75
FEATURE [Part::Ellipsoid] Ellipsoid058
  Angle1 = -90
  Angle2 = 90
  Angle3 = 360
  AttacherType = Attacher::AttachEngine3D
  Placement = pos=(4,5,22) rot=(0.57735,-0.57735,-0.57735;4.18879rad)
  Radius1 = 0.5
  Radius2 = 2
  Radius3 = 0.75
FEATURE [Part::Ellipsoid] Ellipsoid059
  Angle1 = -90
  Angle2 = 90
  Angle3 = 360
  AttacherType = Attacher::AttachEngine3D
  Placement = pos=(5,6,22) rot=(0,1,0;1.5708rad)
  Radius1 = 0.5
  Radius2 = 2
  Radius3 = 0.75
FEATURE [Part::Ellipsoid] Ellipsoid060
  Angle1 = -90
  Angle2 = 90
  Angle3 = 360
  AttacherType = Attacher::AttachEngine3D
  Placement = pos=(6,5,22) rot=(0.57735,-0.57735,-0.57735;4.18879rad)
  Radius1 = 0.5
  Radius2 = 2
  Radius3 = 0.75
FEATURE [Part::Ellipsoid] Ellipsoid061
  Angle1 = -90
  Angle2 = 90
  Angle3 = 360
  AttacherType = Attacher::AttachEngine3D
  Placement = pos=(5,4,22) rot=(0,1,0;1.5708rad)
  Radius1 = 0.5
  Radius2 = 2
  Radius3 = 0.75
FEATURE [Part::Ellipsoid] Ellipsoid062
  Angle1 = -90
  Angle2 = 90
  Angle3 = 360
  AttacherType = Attacher::AttachEngine3D
  Placement = pos=(4,5,22) rot=(0.57735,-0.57735,-0.57735;4.18879rad)
  Radius1 = 0.5
  Radius2 = 2
  Radius3 = 0.75
FEATURE [Part::Ellipsoid] Ellipsoid063
  Angle1 = -90
  Angle2 = 90
  Angle3 = 360
  AttacherType = Attacher::AttachEngine3D
  Placement = pos=(5,6,22) rot=(0,1,0;1.5708rad)
  Radius1 = 0.5
  Radius2 = 2
  Radius3 = 0.75
FEATURE [Part::Ellipsoid] Ellipsoid064
  Angle1 = -90
  Angle2 = 90
  Angle3 = 360
  AttacherType = Attacher::AttachEngine3D
  Placement = pos=(6,5,22) rot=(0.57735,-0.57735,-0.57735;4.18879rad)
  Radius1 = 0.5
  Radius2 = 2
  Radius3 = 0.75
FEATURE [Part::Ellipsoid] Ellipsoid065
  Angle1 = -90
  Angle2 = 90
  Angle3 = 360
  AttacherType = Attacher::AttachEngine3D
  Placement = pos=(5,4,22) rot=(0,1,0;1.5708rad)
  Radius1 = 0.5
  Radius2 = 2
  Radius3 = 0.75
FEATURE [Part::Ellipsoid] Ellipsoid066
  Angle1 = -90
  Angle2 = 90
  Angle3 = 360
  AttacherType = Attacher::AttachEngine3D
  Placement = pos=(4,5,22) rot=(0.57735,-0.57735,-0.57735;4.18879rad)
  Radius1 = 0.5
  Radius2 = 2
  Radius3 = 0.75
FEATURE [Part::Ellipsoid] Ellipsoid067
  Angle1 = -90
  Angle2 = 90
  Angle3 = 360
  AttacherType = Attacher::AttachEngine3D
  Placement = pos=(5,6,22) rot=(0,1,0;1.5708rad)
  Radius1 = 0.5
  Radius2 = 2
  Radius3 = 0.75
FEATURE [Part::Ellipsoid] Ellipsoid068
  Angle1 = -90
  Angle2 = 90
  Angle3 = 360
  AttacherType = Attacher::AttachEngine3D
  Placement = pos=(6,5,22) rot=(0.57735,-0.57735,-0.57735;4.18879rad)
  Radius1 = 0.5
  Radius2 = 2
  Radius3 = 0.75
FEATURE [Part::Ellipsoid] Ellipsoid069
  Angle1 = -90
  Angle2 = 90
  Angle3 = 360
  AttacherType = Attacher::AttachEngine3D
  Placement = pos=(5,4,22) rot=(0,1,0;1.5708rad)
  Radius1 = 0.5
  Radius2 = 2
  Radius3 = 0.75
FEATURE [Part::Ellipsoid] Ellipsoid070
  Angle1 = -90
  Angle2 = 90
  Angle3 = 360
  AttacherType = Attacher::AttachEngine3D
  Placement = pos=(4,5,22) rot=(0.57735,-0.57735,-0.57735;4.18879rad)
  Radius1 = 0.5
  Radius2 = 2
  Radius3 = 0.75
FEATURE [Part::Ellipsoid] Ellipsoid071
  Angle1 = -90
  Angle2 = 90
  Angle3 = 360
  AttacherType = Attacher::AttachEngine3D
  Placement = pos=(5,6,22) rot=(0,1,0;1.5708rad)
  Radius1 = 0.5
  Radius2 = 2
  Radius3 = 0.75
FEATURE [Part::Ellipsoid] Ellipsoid072
  Angle1 = -90
  Angle2 = 90
  Angle3 = 360
  AttacherType = Attacher::AttachEngine3D
  Placement = pos=(6,5,22) rot=(0.57735,-0.57735,-0.57735;4.18879rad)
  Radius1 = 0.5
  Radius2 = 2
  Radius3 = 0.75
FEATURE [Part::Ellipsoid] Ellipsoid073
  Angle1 = -90
  Angle2 = 90
  Angle3 = 360
  AttacherType = Attacher::AttachEngine3D
  Placement = pos=(5,4,22) rot=(0,1,0;1.5708rad)
  Radius1 = 0.5
  Radius2 = 2
  Radius3 = 0.75
FEATURE [Part::Ellipsoid] Ellipsoid074
  Angle1 = -90
  Angle2 = 90
  Angle3 = 360
  AttacherType = Attacher::AttachEngine3D
  Placement = pos=(4,5,22) rot=(0.57735,-0.57735,-0.57735;4.18879rad)
  Radius1 = 0.5
  Radius2 = 2
  Radius3 = 0.75
FEATURE [Part::Ellipsoid] Ellipsoid075
  Angle1 = -90
  Angle2 = 90
  Angle3 = 360
  AttacherType = Attacher::AttachEngine3D
  Placement = pos=(5,6,22) rot=(0,1,0;1.5708rad)
  Radius1 = 0.5
  Radius2 = 2
  Radius3 = 0.75
FEATURE [Part::Ellipsoid] Ellipsoid076
  Angle1 = -90
  Angle2 = 90
  Angle3 = 360
  AttacherType = Attacher::AttachEngine3D
  Placement = pos=(6,5,22) rot=(0.57735,-0.57735,-0.57735;4.18879rad)
  Radius1 = 0.5
  Radius2 = 2
  Radius3 = 0.75
FEATURE [Part::Ellipsoid] Ellipsoid077
  Angle1 = -90
  Angle2 = 90
  Angle3 = 360
  AttacherType = Attacher::AttachEngine3D
  Placement = pos=(5,4,22) rot=(0,1,0;1.5708rad)
  Radius1 = 0.5
  Radius2 = 2
  Radius3 = 0.75
FEATURE [Part::Ellipsoid] Ellipsoid078
  Angle1 = -90
  Angle2 = 90
  Angle3 = 360
  AttacherType = Attacher::AttachEngine3D
  Placement = pos=(4,5,22) rot=(0.57735,-0.57735,-0.57735;4.18879rad)
  Radius1 = 0.5
  Radius2 = 2
  Radius3 = 0.75
FEATURE [Part::Ellipsoid] Ellipsoid079
  Angle1 = -90
  Angle2 = 90
  Angle3 = 360
  AttacherType = Attacher::AttachEngine3D
  Placement = pos=(5,6,22) rot=(0,1,0;1.5708rad)
  Radius1 = 0.5
  Radius2 = 2
  Radius3 = 0.75
FEATURE [Part::Ellipsoid] Ellipsoid080
  Angle1 = -90
  Angle2 = 90
  Angle3 = 360
  AttacherType = Attacher::AttachEngine3D
  Placement = pos=(6,5,22) rot=(0.57735,-0.57735,-0.57735;4.18879rad)
  Radius1 = 0.5
  Radius2 = 2
  Radius3 = 0.75
FEATURE [Part::Ellipsoid] Ellipsoid081
  Angle1 = -90
  Angle2 = 90
  Angle3 = 360
  AttacherType = Attacher::AttachEngine3D
  Placement = pos=(5,4,22) rot=(0,1,0;1.5708rad)
  Radius1 = 0.5
  Radius2 = 2
  Radius3 = 0.75
FEATURE [Part::Ellipsoid] Ellipsoid082
  Angle1 = -90
  Angle2 = 90
  Angle3 = 360
  AttacherType = Attacher::AttachEngine3D
  Placement = pos=(4,5,22) rot=(0.57735,-0.57735,-0.57735;4.18879rad)
  Radius1 = 0.5
  Radius2 = 2
  Radius3 = 0.75
FEATURE [Part::Ellipsoid] Ellipsoid083
  Angle1 = -90
  Angle2 = 90
  Angle3 = 360
  AttacherType = Attacher::AttachEngine3D
  Placement = pos=(5,6,22) rot=(0,1,0;1.5708rad)
  Radius1 = 0.5
  Radius2 = 2
  Radius3 = 0.75
FEATURE [Part::Ellipsoid] Ellipsoid084
  Angle1 = -90
  Angle2 = 90
  Angle3 = 360
  AttacherType = Attacher::AttachEngine3D
  Placement = pos=(6,5,22) rot=(0.57735,-0.57735,-0.57735;4.18879rad)
  Radius1 = 0.5
  Radius2 = 2
  Radius3 = 0.75
FEATURE [Part::Ellipsoid] Ellipsoid085
  Angle1 = -90
  Angle2 = 90
  Angle3 = 360
  AttacherType = Attacher::AttachEngine3D
  Placement = pos=(5,4,22) rot=(0,1,0;1.5708rad)
  Radius1 = 0.5
  Radius2 = 2
  Radius3 = 0.75
FEATURE [Part::Ellipsoid] Ellipsoid086
  Angle1 = -90
  Angle2 = 90
  Angle3 = 360
  AttacherType = Attacher::AttachEngine3D
  Placement = pos=(4,5,22) rot=(0.57735,-0.57735,-0.57735;4.18879rad)
  Radius1 = 0.5
  Radius2 = 2
  Radius3 = 0.75
FEATURE [Part::Ellipsoid] Ellipsoid087
  Angle1 = -90
  Angle2 = 90
  Angle3 = 360
  AttacherType = Attacher::AttachEngine3D
  Placement = pos=(5,6,22) rot=(0,1,0;1.5708rad)
  Radius1 = 0.5
  Radius2 = 2
  Radius3 = 0.75
FEATURE [Part::Ellipsoid] Ellipsoid088
  Angle1 = -90
  Angle2 = 90
  Angle3 = 360
  AttacherType = Attacher::AttachEngine3D
  Placement = pos=(6,5,22) rot=(0.57735,-0.57735,-0.57735;4.18879rad)
  Radius1 = 0.5
  Radius2 = 2
  Radius3 = 0.75
FEATURE [Part::Fillet] Fillet025
  Base = -> Cylinder025
  Edges = 1 edges r=1: [Edge3]
  Placement = pos=(0,0,5) rot=(0,0,1;0rad)
FEATURE [Part::Fillet] Fillet027
  Base = -> Cylinder027
  Edges = 1 edges r=1: [Edge3]
  Placement = pos=(0,0,5) rot=(0,0,1;0rad)
FEATURE [Part::Fillet] Fillet029
  Base = -> Cylinder029
  Edges = 1 edges r=1: [Edge3]
  Placement = pos=(0,0,5) rot=(0,0,1;0rad)
FEATURE [Part::Fillet] Fillet031
  Base = -> Cylinder031
  Edges = 1 edges r=1: [Edge3]
  Placement = pos=(0,0,5) rot=(0,0,1;0rad)
FEATURE [Part::Fillet] Fillet033
  Base = -> Cylinder033
  Edges = 1 edges r=1: [Edge3]
  Placement = pos=(0,0,5) rot=(0,0,1;0rad)
FEATURE [Part::Fillet] Fillet035
  Base = -> Cylinder035
  Edges = 1 edges r=1: [Edge3]
  Placement = pos=(0,0,5) rot=(0,0,1;0rad)
FEATURE [Part::Fillet] Fillet037
  Base = -> Cylinder037
  Edges = 1 edges r=1: [Edge3]
  Placement = pos=(0,0,5) rot=(0,0,1;0rad)
FEATURE [Part::Fillet] Fillet039
  Base = -> Cylinder039
  Edges = 1 edges r=1: [Edge3]
  Placement = pos=(0,0,5) rot=(0,0,1;0rad)
FEATURE [Part::MultiFuse] Fusion033
  Placement = pos=(-1,-1,-10) rot=(0,0,1;0rad)
  Refine = true
  Shapes = -> [Ellipsoid060,Cylinder024,Ellipsoid057,Ellipsoid058,Ellipsoid059]
FEATURE [Part::Fillet] Fillet026
  Base = -> Fusion033
  Edges = 1 edges r=1: [Edge7]
  Placement = pos=(0,0,4) rot=(0,0,1;0rad)
FEATURE [Part::MultiFuse] Fusion034
  Placement = pos=(-1,-1,-10) rot=(0,0,1;0rad)
  Refine = true
  Shapes = -> [Ellipsoid064,Cylinder026,Ellipsoid061,Ellipsoid062,Ellipsoid063]
FEATURE [Part::Fillet] Fillet028
  Base = -> Fusion034
  Edges = 1 edges r=1: [Edge7]
  Placement = pos=(0,0,4) rot=(0,0,1;0rad)
FEATURE [Part::MultiFuse] Fusion035
  Placement = pos=(-1,-1,-10) rot=(0,0,1;0rad)
  Refine = true
  Shapes = -> [Ellipsoid068,Cylinder028,Ellipsoid065,Ellipsoid066,Ellipsoid067]
FEATURE [Part::Fillet] Fillet030
  Base = -> Fusion035
  Edges = 1 edges r=1: [Edge7]
  Placement = pos=(0,0,4) rot=(0,0,1;0rad)
FEATURE [Part::MultiFuse] Fusion036
  Placement = pos=(-1,-1,-10) rot=(0,0,1;0rad)
  Refine = true
  Shapes = -> [Ellipsoid072,Cylinder030,Ellipsoid069,Ellipsoid070,Ellipsoid071]
FEATURE [Part::Fillet] Fillet032
  Base = -> Fusion036
  Edges = 1 edges r=1: [Edge7]
  Placement = pos=(0,0,4) rot=(0,0,1;0rad)
FEATURE [Part::MultiFuse] Fusion037  label="Pilar_PCB_1.6mm_3mm006"
  Refine = true
  Shapes = -> [Fillet025,Fillet026,Fillet027,Fillet028,Fillet029,Fillet030,Fillet031,Fillet032]
FEATURE [Part::MultiFuse] Fusion038
  Placement = pos=(-1,-1,-10) rot=(0,0,1;0rad)
  Refine = true
  Shapes = -> [Ellipsoid076,Cylinder032,Ellipsoid073,Ellipsoid074,Ellipsoid075]
FEATURE [Part::Fillet] Fillet034
  Base = -> Fusion038
  Edges = 1 edges r=1: [Edge7]
  Placement = pos=(0,0,4) rot=(0,0,1;0rad)
FEATURE [Part::MultiFuse] Fusion039
  Placement = pos=(-1,-1,-10) rot=(0,0,1;0rad)
  Refine = true
  Shapes = -> [Ellipsoid080,Cylinder034,Ellipsoid077,Ellipsoid078,Ellipsoid079]
FEATURE [Part::Fillet] Fillet036
  Base = -> Fusion039
  Edges = 1 edges r=1: [Edge7]
  Placement = pos=(0,0,4) rot=(0,0,1;0rad)
FEATURE [Part::MultiFuse] Fusion040
  Placement = pos=(-1,-1,-10) rot=(0,0,1;0rad)
  Refine = true
  Shapes = -> [Ellipsoid084,Cylinder036,Ellipsoid081,Ellipsoid082,Ellipsoid083]
FEATURE [Part::Fillet] Fillet038
  Base = -> Fusion040
  Edges = 1 edges r=1: [Edge7]
  Placement = pos=(0,0,4) rot=(0,0,1;0rad)
FEATURE [Part::MultiFuse] Fusion041
  Placement = pos=(-1,-1,-10) rot=(0,0,1;0rad)
  Refine = true
  Shapes = -> [Ellipsoid088,Cylinder038,Ellipsoid085,Ellipsoid086,Ellipsoid087]
FEATURE [Part::Fillet] Fillet040
  Base = -> Fusion041
  Edges = 1 edges r=1: [Edge7]
  Placement = pos=(0,0,4) rot=(0,0,1;0rad)
FEATURE [Part::MultiFuse] Fusion042  label="Pilar_PCB_1.6mm_3mm007"
  Placement = pos=(0,20,0) rot=(0,0,1;0rad)
  Refine = true
  Shapes = -> [Fillet033,Fillet034,Fillet035,Fillet036,Fillet037,Fillet038,Fillet039,Fillet040]
FEATURE [Part::MultiFuse] Fusion043  label="Suport_SSR_2A"
  Placement = pos=(14.7521,82.0362,0) rot=(0,0,1;0rad)
  Refine = true
  Shapes = -> [Fusion027,Fusion032,Fusion037,Fusion042]
FEATURE [Part::Feature] Part__Feature141  label="Alusplaat"
  shape: bbox 2 x 8 x 2 mm, 3 faces (baked)
FEATURE [Part::Feature] Part__Feature142  label="Alusplaat001"
  shape: bbox 34.5 x 25.5 x 22 mm, 49 faces (baked)
FEATURE [Part::Feature] Part__Feature143  label="2-pin screw terminal"
  Placement = pos=(5.975,-10,-1.55) rot=(0,0.707107,0.707107;3.14159rad)
  shape: bbox 3.621 x 3.681 x 1.007 mm, 128 faces (baked)
FEATURE [Part::Feature] Part__Feature144  label="2-pin screw terminal001"
  Placement = pos=(5.975,-10,-1.55) rot=(0,0.707107,0.707107;3.14159rad)
  shape: bbox 7.5 x 10 x 13.4 mm, 120 faces (baked)
FEATURE [Part::Feature] Part__Feature145  label="2-pin screw terminal002"
  Placement = pos=(5.975,-10,-1.55) rot=(0,0.707107,0.707107;3.14159rad)
  shape: bbox 3.621 x 3.681 x 1.007 mm, 128 faces (baked)
FEATURE [Part::Feature] Part__Feature146  label="3-pin screw terminal"
  Placement = pos=(-10.475,7.5,-1.55) rot=(1,0,0;1.5708rad)
  shape: bbox 7.5 x 15 x 13.4 mm, 176 faces (baked)
FEATURE [Part::Feature] Part__Feature147  label="3-pin screw terminal001"
  Placement = pos=(-10.475,7.5,-1.55) rot=(1,0,0;1.5708rad)
  shape: bbox 3.621 x 3.681 x 1.007 mm, 128 faces (baked)
FEATURE [Part::Feature] Part__Feature148  label="3-pin screw terminal002"
  Placement = pos=(-10.475,7.5,-1.55) rot=(1,0,0;1.5708rad)
  shape: bbox 3.621 x 3.681 x 1.007 mm, 128 faces (baked)
FEATURE [Part::Feature] Part__Feature149  label="3-pin screw terminal003"
  Placement = pos=(-10.475,7.5,-1.55) rot=(1,0,0;1.5708rad)
  shape: bbox 3.621 x 3.681 x 1.007 mm, 128 faces (baked)
FEATURE [App::Part] Assem1  label="SSR2A_RY"
  Group = -> [Part__Feature141,Part__Feature142,Part__Feature143,Part__Feature144,Part__Feature145,Part__Feature146,Part__Feature147,Part__Feature148,Part__Feature149]
  Origin = -> Origin022
  Placement = pos=(33,96,15) rot=(0,0,1;0rad)
FEATURE [Part::Feature] Part__Feature  label="BreadBoard"
  Placement = pos=(123.666,85.9377,3) rot=(1,0,0;1.5708rad)
  shape: bbox 83.8 x 55.5 x 8.01 mm, 3672 faces, 3 solids (baked)
FEATURE [Part::MultiFuse] Fusion015
  Placement = pos=(0,47,0) rot=(0,0,1;0rad)
  Refine = true
  Shapes = -> [Box008,Box009,Ellipsoid023]
FEATURE [Part::MultiFuse] Fusion044  label="Suport_Alimentació"
  Placement = pos=(16.2464,2.88824,0) rot=(0,0,1;0rad)
  Refine = true
  Shapes = -> [Fusion014,Fusion015]
FEATURE [Part::Box] Box010  label="PS_PCB(REF)"
  AttacherType = Attacher::AttachEngine3D
  Height = 1.6
  Length = 23
  Placement = pos=(35,52,13) rot=(0,0,1;1.5708rad)
  Width = 18
FEATURE [Part::MultiFuse] Fusion045
  Refine = true
  Shapes = -> [Fusion044,Fusion043,Fillet016,Fusion013,Box]
FEATURE [Part::Fillet] Fillet041
  Base = -> Fusion045
  Edges = 20 edges r=1: [Edge10,Edge11,Edge12,Edge13,Edge14,Edge15,Edge16,Edge17,Edge18,Edge19,Edge20,Edge21,Edge26,Edge27,Edge28,Edge29,Edge30,Edge31,Edge32,Edge33]
FEATURE [Part::Fillet] Fillet042
  Base = -> Fillet041
  Edges = 1 edges r=3: [Edge10]
FEATURE [Part::Fillet] Fillet043
  Base = -> Fillet042
  Edges = 4 edges r=1: [Edge11,Edge12,Edge13,Edge14]
